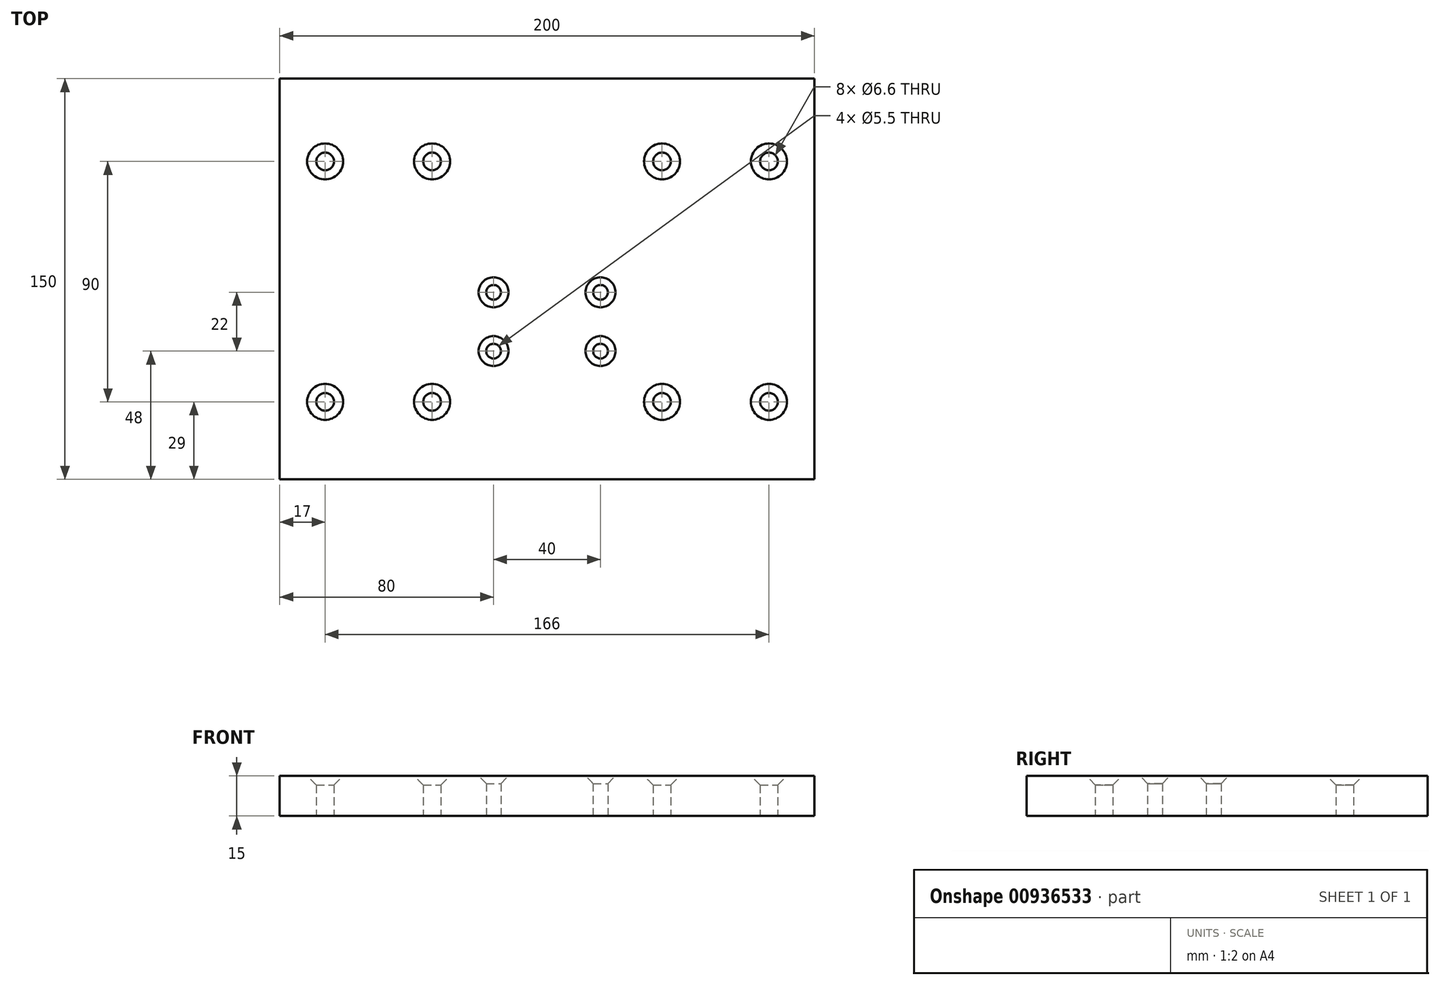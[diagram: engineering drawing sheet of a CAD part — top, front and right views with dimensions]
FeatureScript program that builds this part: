
annotation { "Feature Type Name" : "Feature", "Feature Type Description" : "" }
export const myFeature = defineFeature(function(context is Context, id is Id, definition is map)
    precondition{}
    {
        {
            var Q0;
            Q0=qCreatedBy(makeId("Top.planeOp"),FACE);
            var sketch = newSketch(context, id + "F0", { "sketchPlane" : qUnion([Q0])});
            skLineSegment(sketch, "E0.bottom", {"start": v(100, 75) * mm, "end": v(-100, 75) * mm});
            skLineSegment(sketch, "E0.top", {"start": v(100, -75) * mm, "end": v(-100, -75) * mm});
            skLineSegment(sketch, "E0.left", {"start": v(100, 75) * mm, "end": v(100, -75) * mm});
            skLineSegment(sketch, "E0.right", {"start": v(-100, 75) * mm, "end": v(-100, -75) * mm});
            skPoint(sketch, "E0.middle", {"position": v(0, 0) * mm});
            skSolve(sketch);
        }
        {
            var Q0;
            Q0=qSketchRegion(id+"F0",true);
            extrude(context, id + "F1", {"entities" : qUnion([Q0]), "depth" : 15 * mm, "offsetDistance" : 25 * mm});
        }
        {
            var Q0;
            Q0=makeQuery(id+"F1.opExtrude","CAP_FACE",FACE,{"disambiguationData":[OSD([sQuery(id+"F0.wireOp",EDGE,"E0.bottom"),sQuery(id+"F0.wireOp",EDGE,"E0.top"),sQuery(id+"F0.wireOp",EDGE,"E0.left"),sQuery(id+"F0.wireOp",EDGE,"E0.right")])],"isStart":false});
            var sketch = newSketch(context, id + "F2", { "sketchPlane" : qUnion([Q0])});
            skPoint(sketch, "E1", {"position": v(-83, 44) * mm});
            skPoint(sketch, "E2", {"position": v(-43, 44) * mm});
            skPoint(sketch, "E3", {"position": v(-83, -46) * mm});
            skPoint(sketch, "E4", {"position": v(-43, -46) * mm});
            skPoint(sketch, "E5.MirrorP", {"position": v(83, 44) * mm});
            skPoint(sketch, "E6.MirrorP", {"position": v(43, 44) * mm});
            skPoint(sketch, "E7.MirrorP", {"position": v(83, -46) * mm});
            skPoint(sketch, "E8.MirrorP", {"position": v(43, -46) * mm});
            skPoint(sketch, "E9", {"position": v(-20, -5) * mm});
            skPoint(sketch, "E10", {"position": v(-20, -27) * mm});
            skPoint(sketch, "E11.MirrorP", {"position": v(20, -5) * mm});
            skPoint(sketch, "E12.MirrorP", {"position": v(20, -27) * mm});
            skSolve(sketch);
        }
        {
            var Q0;
            Q0=sQuery(id+"F2.wireOp",VERTEX,"E1");
            var Q1;
            Q1=sQuery(id+"F2.wireOp",VERTEX,"E2");
            var Q2;
            Q2=sQuery(id+"F2.wireOp",VERTEX,"E3");
            var Q3;
            Q3=sQuery(id+"F2.wireOp",VERTEX,"E4");
            var Q4;
            Q4=sQuery(id+"F2.wireOp",VERTEX,"E6.MirrorP");
            var Q5;
            Q5=sQuery(id+"F2.wireOp",VERTEX,"E5.MirrorP");
            var Q6;
            Q6=sQuery(id+"F2.wireOp",VERTEX,"E8.MirrorP");
            var Q7;
            Q7=sQuery(id+"F2.wireOp",VERTEX,"E7.MirrorP");
            var Q8;
            Q8=makeQuery(id+"F1.opExtrude","SWEPT_BODY",BODY,{"disambiguationData":[OSD([sQuery(id+"F0.wireOp",EDGE,"E0.bottom"),sQuery(id+"F0.wireOp",EDGE,"E0.top"),sQuery(id+"F0.wireOp",EDGE,"E0.left"),sQuery(id+"F0.wireOp",EDGE,"E0.right")])]});
            hole(context, id + "F3", {"style" : HoleStyle.C_SINK, "endStyle" : HoleEndStyle.THROUGH, "standardTappedOrClearance" : lookupTablePath({ "fit" : "Normal", "standard" : "ISO", "size" : "M6", "type" : "Clearance" }), "standardBlindInLast" : lookupTablePath({ "fit" : "Normal", "standard" : "ISO", "engagement" : "75%", "pitch" : "1 mm", "size" : "M6", "type" : "Clearance & tapped" }), "holeDiameter" : 6.6 * mm, "cSinkDiameter" : 13.44 * mm, "cSinkAngle" : 90 * degree, "majorDiameter" : 5 * mm, "tappedDepth" : 12 * mm, "tapClearance" : 3, "locations" : qUnion([Q0, Q1, Q2, Q3, Q4, Q5, Q6, Q7]), "scope" : qUnion([Q8]), "startStyle" : HoleStartStyle.PART});
        }
        {
            var Q0;
            Q0=sQuery(id+"F2.wireOp",VERTEX,"E10");
            var Q1;
            Q1=sQuery(id+"F2.wireOp",VERTEX,"E9");
            var Q2;
            Q2=sQuery(id+"F2.wireOp",VERTEX,"E11.MirrorP");
            var Q3;
            Q3=sQuery(id+"F2.wireOp",VERTEX,"E12.MirrorP");
            var Q4;
            Q4=makeQuery(id+"F1.opExtrude","SWEPT_BODY",BODY,{"disambiguationData":[OSD([sQuery(id+"F0.wireOp",EDGE,"E0.bottom"),sQuery(id+"F0.wireOp",EDGE,"E0.top"),sQuery(id+"F0.wireOp",EDGE,"E0.left"),sQuery(id+"F0.wireOp",EDGE,"E0.right")])]});
            hole(context, id + "F4", {"style" : HoleStyle.C_SINK, "endStyle" : HoleEndStyle.THROUGH, "standardTappedOrClearance" : lookupTablePath({ "fit" : "Normal", "standard" : "ISO", "size" : "M5", "type" : "Clearance" }), "standardBlindInLast" : lookupTablePath({ "fit" : "Normal", "standard" : "ISO", "engagement" : "75%", "pitch" : "0.8 mm", "size" : "M5", "type" : "Clearance & tapped" }), "holeDiameter" : 5.5 * mm, "cSinkDiameter" : 11.2 * mm, "cSinkAngle" : 90 * degree, "majorDiameter" : 5 * mm, "tappedDepth" : 12 * mm, "tapClearance" : 3, "locations" : qUnion([Q0, Q1, Q2, Q3]), "scope" : qUnion([Q4]), "startStyle" : HoleStartStyle.PART});
        }
    });
